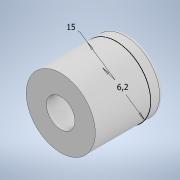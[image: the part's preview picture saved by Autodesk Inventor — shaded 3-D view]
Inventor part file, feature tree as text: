
AUTODESK INVENTOR PART (.ipt)
format: ipt  version: 2022.2 (Build 262287010, 287A)  size: 115,712 bytes
history: native  units: mm
features: extrude x2, sketch x1, fillet x1
ambient origin geometry x8: Origin, YZ Plane, XZ Plane, XY Plane, X Axis, Y Axis, Z Axis, Center Point
bodies: Volumenkörper1 (feature_tree)
feature tree (4):
  sketch  "Skizze1"  dims[d0=6.2mm d1=15.0mm d2=12.0mm d3=0.0mm d4=3.0mm d5=0.0mm d6=1.0mm]
  extrude  "Extrusion1"  Depth=15.0mm
  extrude  "Extrusion2"  Depth=12.0mm TaperAngle=0.0deg
  fillet  "Rundung1"  Radius=3.0mm
